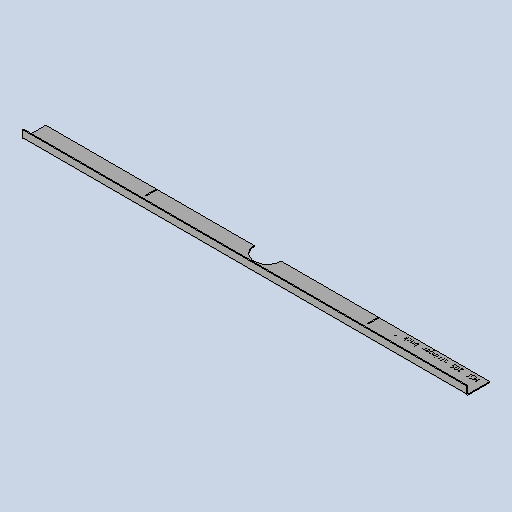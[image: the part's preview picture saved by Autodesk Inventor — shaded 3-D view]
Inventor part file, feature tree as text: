
AUTODESK INVENTOR PART (.ipt)
format: ipt  version: 2025 (Build 290162010, 162A)  size: 257,024 bytes
history: native  units: mm
features: other x5, sheet_metal_op x4, sketch x4, extrude x1
ambient origin geometry x8: Origin, YZ Plane, XZ Plane, XY Plane, X Axis, Y Axis, Z Axis, Center Point
bodies: Solid1 (feature_tree)
feature tree (14):
  sheet_metal_op  "Face1"
  sheet_metal_op  "Flange1"
  extrude  "Extrusion4"  Depth=52.0mm
  other  "Mark3"
  other  "A-Side Definition"
  sketch  "Sketch1"  dims[d0=980.0mm d1=52.0mm]
  other  "Plate1"
  sketch  "Sketch2"  dims[d2=2.0mm]
  other  "Plate2"
  sheet_metal_op  "Bend1"
  sheet_metal_op  "Corner1"
  sketch  "Sketch9"  dims[d3=2.0mm]
  sketch  "Sketch11"  dims[d4=1.0mm d5=4.0mm d6=2.75mm d7=20.0mm d8=90.0deg d9=2.75mm d10=8.0mm d11=2.0mm d12=2.75mm d38=200.0mm d39=12.0mm d42=5.0mm d43=5.0mm d44=60.0mm d45=0.0mm d46=0.0mm d47=2.1mm d49=490.0mm d50=29.0mm]
  other  "Definition1"
